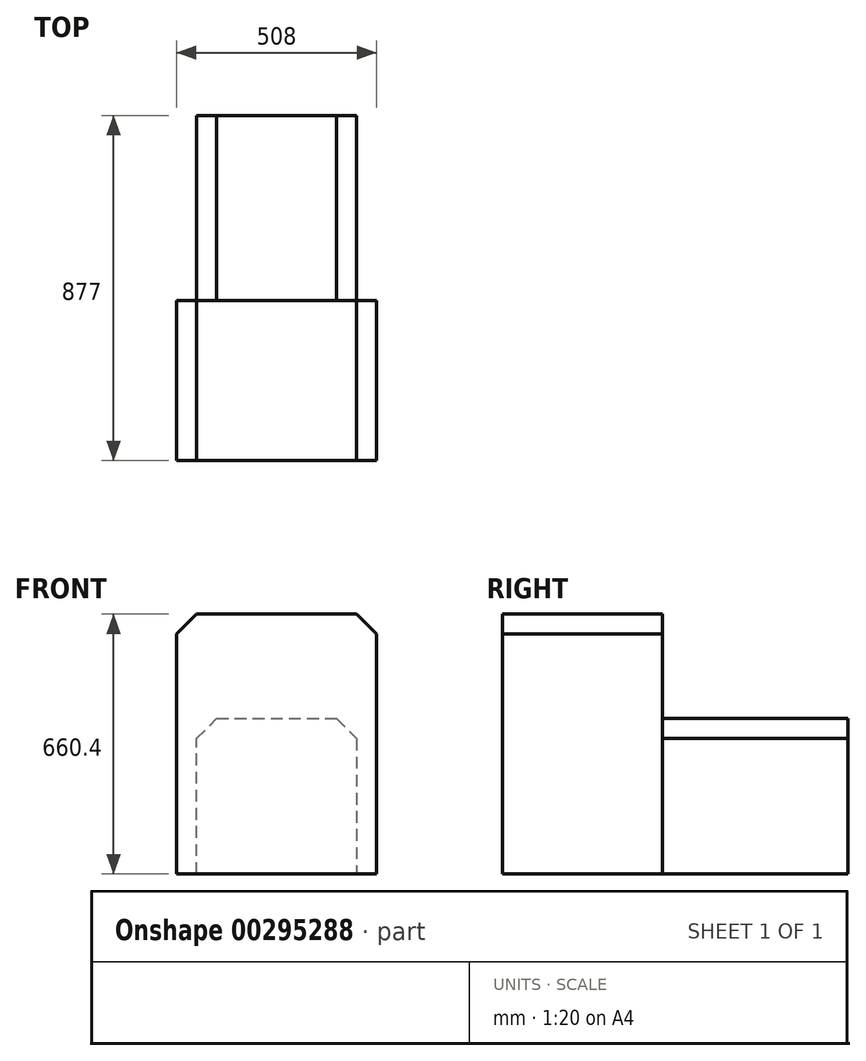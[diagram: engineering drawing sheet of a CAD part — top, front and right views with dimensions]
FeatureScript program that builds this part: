
annotation { "Feature Type Name" : "Feature", "Feature Type Description" : "" }
export const myFeature = defineFeature(function(context is Context, id is Id, definition is map)
    precondition{}
    {
        {
            var Q0;
            Q0=qCreatedBy(makeId("Front.planeOp"),FACE);
            var sketch = newSketch(context, id + "F0", { "sketchPlane" : qUnion([Q0])});
            skLineSegment(sketch, "E0", {"start": v(-200.08, -204.08) * mm, "end": v(-200.08, 140.11) * mm});
            skLineSegment(sketch, "E1", {"start": v(-200.08, 140.11) * mm, "end": v(-149.28, 190.91) * mm});
            skLineSegment(sketch, "E2", {"start": v(-149.28, 190.91) * mm, "end": v(155.52, 190.91) * mm});
            skLineSegment(sketch, "E3", {"start": v(155.52, 190.91) * mm, "end": v(206.32, 140.11) * mm});
            skLineSegment(sketch, "E4", {"start": v(206.32, 140.11) * mm, "end": v(206.32, -204.08) * mm});
            skLineSegment(sketch, "E5", {"start": v(206.32, -204.08) * mm, "end": v(-200.08, -204.08) * mm});
            skSolve(sketch);
        }
        {
            var Q0;
            Q0 = qSketchRegion(id + "F0", true);
            extrude(context, id + "F1", {"entities" : qUnion([Q0]), "depth" : 877 * mm});
        }
        {
            var Q0;
            Q0=makeQuery(id+"F1.opExtrude","CAP_FACE",FACE,{"disambiguationData":[OSD([sQuery(id+"F0.wireOp",EDGE,"E0"),sQuery(id+"F0.wireOp",EDGE,"E1"),sQuery(id+"F0.wireOp",EDGE,"E2"),sQuery(id+"F0.wireOp",EDGE,"E3"),sQuery(id+"F0.wireOp",EDGE,"E4"),sQuery(id+"F0.wireOp",EDGE,"E5")])],"isStart":false});
            var sketch = newSketch(context, id + "F2", { "sketchPlane" : qUnion([Q0])});
            skLineSegment(sketch, "E6", {"start": v(-250.88, -204.08) * mm, "end": v(257.12, -204.08) * mm});
            skLineSegment(sketch, "E7", {"start": v(257.12, -204.08) * mm, "end": v(257.12, 405.52) * mm});
            skLineSegment(sketch, "E8", {"start": v(257.12, 405.52) * mm, "end": v(206.32, 456.32) * mm});
            skLineSegment(sketch, "E9", {"start": v(206.32, 456.32) * mm, "end": v(-200.08, 456.32) * mm});
            skLineSegment(sketch, "E10", {"start": v(-200.08, 456.32) * mm, "end": v(-250.88, 405.52) * mm});
            skLineSegment(sketch, "E11", {"start": v(-250.88, 405.52) * mm, "end": v(-250.88, -204.08) * mm});
            skSolve(sketch);
        }
        {
            var Q0;
            {var subQ4=sQuery(id+"F2.wireOp",EDGE,"E7");Q0=makeQuery(id+"F2.imprint","IMPRINT",FACE,{"disambiguationData":[TD([[makeQuery(id+"F2.imprint","IMPRINT",EDGE,{"derivedFrom":subQ4}),1.0]])]});}
            extrude(context, id + "F3", {"entities" : qUnion([Q0]), "operationType" : NewBodyOperationType.ADD, "oppositeDirection" : true, "depth" : 406.4 * mm});
        }
    });
